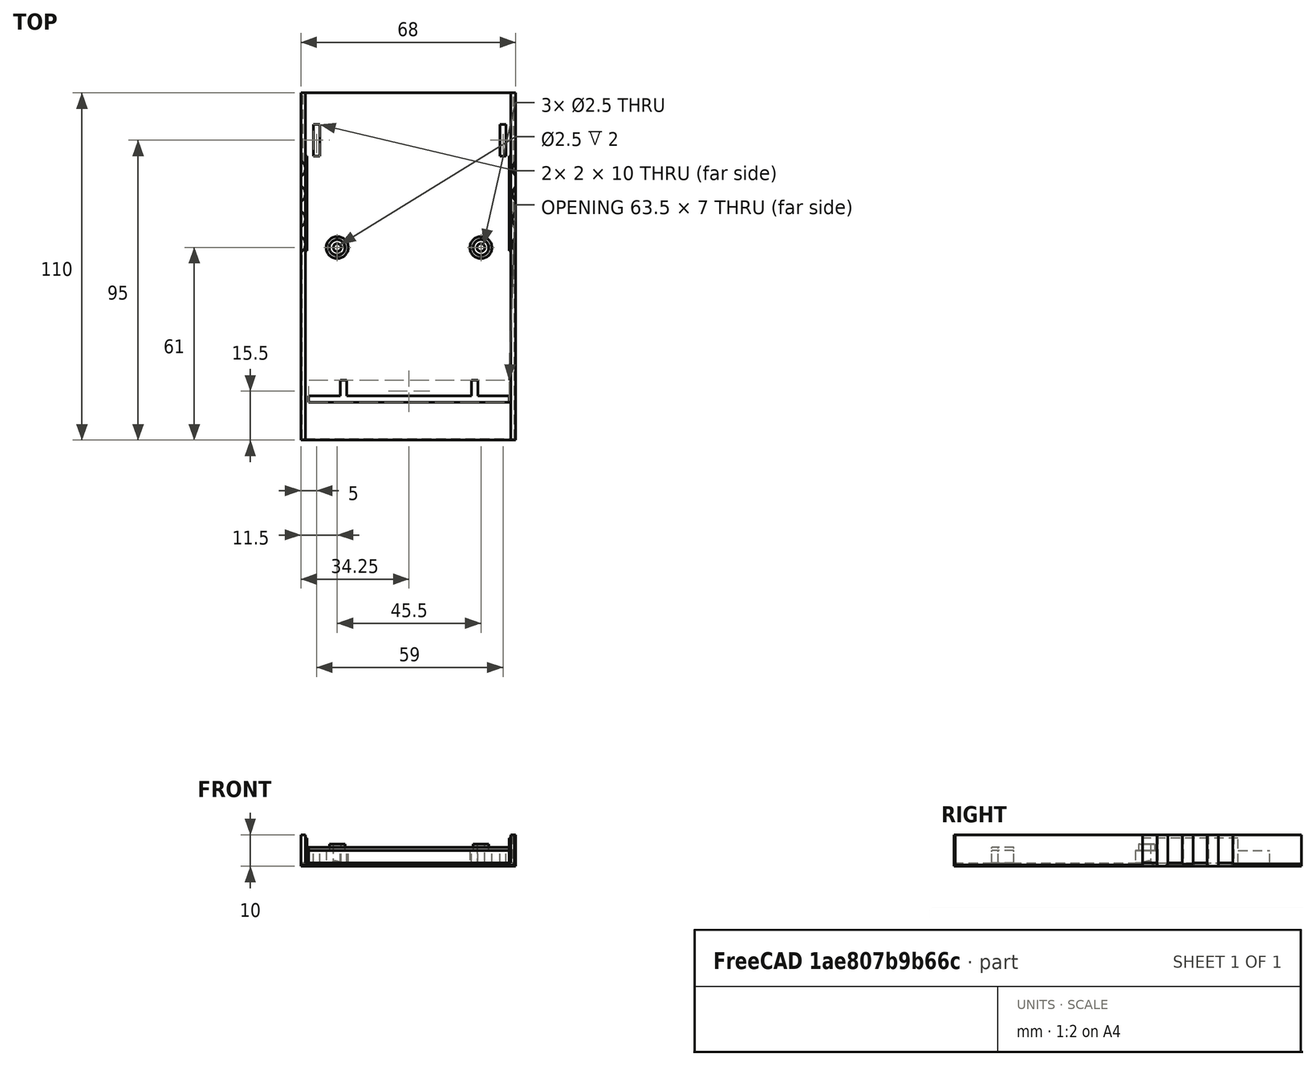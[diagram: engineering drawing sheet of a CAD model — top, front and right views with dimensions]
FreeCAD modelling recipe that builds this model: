
FCSTD DOCUMENT  (FreeCAD 0.20R29410 (Git))
Label: RTO_Cart_Bottom
License: All rights reserved
LicenseURL: http://en.wikipedia.org/wiki/All_rights_reserved
objects: Part::Cylinder×14, Part::MultiFuse×12, Part::Cut×12, Part::Box×7, Part::Chamfer×4, Part::Cone×2, Sketcher::SketchObject×1, PartDesign::Pad×1, PartDesign::Body×1, Mesh::Feature×1, Part::Feature×1
note: 56 computed .brp shape members not serialized (recipe doc carries the construction recipe); baked Part::Feature solids carry a one-line shape summary decoded from their .brp

FEATURE [Part::Cylinder] Cylinder001  label="Cilindro"
  Angle = 360
  AttacherType = Attacher::AttachEngine3D
  FirstAngle = 0
  Height = 16
  Placement = pos=(-11,61,-2) rot=(0,0,1;0rad)
  Radius = 1.25
  SecondAngle = 0
FEATURE [Part::Cylinder] Cylinder002  label="Cilindro001"
  Angle = 360
  AttacherType = Attacher::AttachEngine3D
  FirstAngle = 0
  Height = 20
  Placement = pos=(-56.5,61,-2) rot=(0,0,1;0rad)
  Radius = 1.25
  SecondAngle = 0
FEATURE [Part::Cone] Cone  label="Cono"
  Angle = 360
  AttacherType = Attacher::AttachEngine3D
  Height = 4
  Placement = pos=(-11,61,-1) rot=(0,0,1;3.14159rad)
  Radius1 = 3
  Radius2 = 0
FEATURE [Part::Cone] Cone001  label="Cono001"
  Angle = 360
  AttacherType = Attacher::AttachEngine3D
  Height = 4
  Placement = pos=(-56.7,61.2,-1) rot=(0,0,1;0.017453rad)
  Radius1 = 3
  Radius2 = 0
FEATURE [Part::Box] Box  label="Cubo"
  AttacherType = Attacher::AttachEngine3D
  Height = 4
  Length = 2
  Placement = pos=(-5,90,1) rot=(0,0,1;0rad)
  Width = 10
FEATURE [Part::Box] Box001  label="Cubo001"
  AttacherType = Attacher::AttachEngine3D
  Height = 4
  Length = 2
  Placement = pos=(-64,90,1) rot=(0,0,1;0rad)
  Width = 10
FEATURE [Part::Box] Box004  label="base"
  AttacherType = Attacher::AttachEngine3D
  Height = 1
  Length = 68
  Placement = pos=(-68,0,0) rot=(0,0,1;0rad)
  Width = 110
FEATURE [Part::Cylinder] Cylinder003  label="Cilindro002"
  Angle = 360
  AttacherType = Attacher::AttachEngine3D
  FirstAngle = 0
  Height = 4
  Placement = pos=(-11,61,1) rot=(0,0,1;0rad)
  Radius = 3.5
  SecondAngle = 0
FEATURE [Part::Cylinder] Cylinder004  label="Cilindro003"
  Angle = 360
  AttacherType = Attacher::AttachEngine3D
  FirstAngle = 0
  Height = 3
  Placement = pos=(-11,61,4) rot=(0,0,1;0rad)
  Radius = 2.5
  SecondAngle = 0
FEATURE [Part::Cylinder] Cylinder  label="Cilindro004"
  Angle = 360
  AttacherType = Attacher::AttachEngine3D
  FirstAngle = 0
  Height = 4
  Placement = pos=(-56.5,61,1) rot=(0,0,1;0rad)
  Radius = 3.5
  SecondAngle = 0
FEATURE [Part::Cylinder] Cylinder005  label="Cilindro005"
  Angle = 360
  AttacherType = Attacher::AttachEngine3D
  FirstAngle = 0
  Height = 2
  Placement = pos=(-56.5,61,5) rot=(0,0,1;0rad)
  Radius = 2.5
  SecondAngle = 0
FEATURE [Part::Box] Box005  label="Cubo002"
  AttacherType = Attacher::AttachEngine3D
  Height = 10
  Length = 1.5
  Placement = pos=(-1.5,0,0) rot=(0,0,1;0rad)
  Width = 110
FEATURE [Part::Box] Box006  label="Cubo003"
  AttacherType = Attacher::AttachEngine3D
  Height = 10
  Length = 1.5
  Placement = pos=(-68,0,0) rot=(0,0,1;0rad)
  Width = 110
FEATURE [Sketcher::SketchObject] Sketch004
  AttachmentOffset = pos=(0,0,1) rot=(0,0,1;0rad)
  FullyConstrained = true
  MapMode = 5
  Placement = pos=(0,0,1) rot=(0,0,1;0rad)
  Support = -> [XY_Plane]
  sketch-geometry (12):
    g0: LineSegment StartX=-65.5 StartY=12 StartZ=0 EndX=-2 EndY=12 EndZ=0
    g1: LineSegment StartX=-2 StartY=14 StartZ=0 EndX=-12 EndY=14 EndZ=0
    g2: LineSegment StartX=-12 StartY=19 StartZ=0 EndX=-14 EndY=19 EndZ=0
    g3: LineSegment StartX=-12 StartY=19 StartZ=0 EndX=-12 EndY=14 EndZ=0
    g4: LineSegment StartX=-14 StartY=19 StartZ=0 EndX=-14 EndY=14 EndZ=0
    g5: LineSegment StartX=-14 StartY=14 StartZ=0 EndX=-53.5 EndY=14 EndZ=0
    g6: LineSegment StartX=-53.5 StartY=14 StartZ=0 EndX=-53.5 EndY=19 EndZ=0
    g7: LineSegment StartX=-53.5 StartY=19 StartZ=0 EndX=-55.5 EndY=19 EndZ=0
    g8: LineSegment StartX=-55.5 StartY=19 StartZ=0 EndX=-55.5 EndY=14 EndZ=0
    g9: LineSegment StartX=-55.5 StartY=14 StartZ=0 EndX=-65.5 EndY=14 EndZ=0
    g10: LineSegment StartX=-65.5 StartY=14 StartZ=0 EndX=-65.5 EndY=12 EndZ=0
    g11: LineSegment StartX=-2 StartY=14 StartZ=0 EndX=-2 EndY=12 EndZ=0
  constraints (36):
    c: Horizontal(g0)
    c: Horizontal(g1)
    c: Coincident(g3,g2)
    c: Coincident(g3,g1)
    c: Coincident(g4,g2)
    c: Vertical(g4)
    c: Coincident(g5,g4)
    c: Horizontal(g5)
    c: Coincident(g6,g5)
    c: Vertical(g6)
    c: Coincident(g7,g6)
    c: Coincident(g7,g8)
    c: Vertical(g8)
    c: Coincident(g8,g9)
    c: Horizontal(g9)
    c: Coincident(g9,g10)
    c: Coincident(g10,g0)
    c: Horizontal(g7)
    c: Vertical(g10)
    c: Vertical(g3)
    c: DistanceY(g0,g9) = 2
    c: DistanceX(g7,g7) = 2
    c: DistanceX(g2,g2) = 2
    c: DistanceY(g4,g4) = 5
    c: DistanceY(g0,g1) = 2
    c: DistanceY(g8,g5) = 0
    c: Horizontal(g2)
    c: DistanceX(g0,g0) = 63.5
    c: DistanceX(g9,g9) = 10
    c: DistanceX(g1,g1) = 10
    c: DistanceY(g8,g8) = 5
    c: Coincident(g11,g1)
    c: Coincident(g11,g0)
    c: Vertical(g11)
    c: DistanceY(g-1,g0) = 12
    c: DistanceX(g0,g-1) = 2
FEATURE [PartDesign::Pad] Pad013  label="front_bar"
  Direction = (0,0,1)
  Length = 5
  Length2 = 10
  Profile = -> Sketch004
  ReferenceAxis = -> Sketch004 [N_Axis]
  Type = 0
FEATURE [Part::MultiFuse] Fusion
  Shapes = -> [Box004,Pad013]
FEATURE [Part::MultiFuse] Fusion001
  Shapes = -> [Fusion,Box]
FEATURE [Part::MultiFuse] Fusion002
  Shapes = -> [Fusion001,Box001]
FEATURE [Part::MultiFuse] Fusion003
  Shapes = -> [Fusion002,Cylinder003]
FEATURE [Part::MultiFuse] Fusion004
  Shapes = -> [Fusion003,Cylinder004]
FEATURE [Part::Cut] Cut
  Base = -> Fusion004
  Tool = -> Cylinder001
FEATURE [Part::Cut] Cut001
  Base = -> Cut
  Tool = -> Cone
FEATURE [Part::MultiFuse] Fusion005
  Shapes = -> [Cut001,Cylinder]
FEATURE [Part::MultiFuse] Fusion006
  Shapes = -> [Fusion005,Cylinder005]
FEATURE [Part::Cut] Cut002
  Base = -> Fusion006
  Tool = -> Cylinder002
FEATURE [Part::Cut] Cut003
  Base = -> Cut002
  Tool = -> Cone001
FEATURE [Part::MultiFuse] Fusion007
  Shapes = -> [Cut003,Box005]
FEATURE [Part::MultiFuse] Fusion008
  Shapes = -> [Fusion007,Box006]
FEATURE [PartDesign::Body] Body001  label="slot"
  Group = -> [Sketch004,Pad013]
  Origin = -> Origin
  Placement = pos=(0,0,-1) rot=(0,0,1;0rad)
  Tip = -> Pad013
FEATURE [Part::Cylinder] Cylinder006  label="Cilindro006"
  Angle = 360
  AttacherType = Attacher::AttachEngine3D
  FirstAngle = 0
  Height = 22
  Placement = pos=(2,62,0) rot=(0,0,1;0rad)
  Radius = 3
  SecondAngle = 0
FEATURE [Part::Cylinder] Cylinder007  label="Cilindro007"
  Angle = 360
  AttacherType = Attacher::AttachEngine3D
  FirstAngle = 0
  Height = 22
  Placement = pos=(2,70,0) rot=(0,0,1;0rad)
  Radius = 3
  SecondAngle = 0
FEATURE [Part::Cylinder] Cylinder008  label="Cilindro008"
  Angle = 360
  AttacherType = Attacher::AttachEngine3D
  FirstAngle = 0
  Height = 22
  Placement = pos=(2,78,0) rot=(0,0,1;0rad)
  Radius = 3
  SecondAngle = 0
FEATURE [Part::Cylinder] Cylinder009  label="Cilindro009"
  Angle = 360
  AttacherType = Attacher::AttachEngine3D
  FirstAngle = 0
  Height = 22
  Placement = pos=(2,86,0) rot=(0,0,1;0rad)
  Radius = 3
  SecondAngle = 0
FEATURE [Part::Cylinder] Cylinder010  label="Cilindro010"
  Angle = 360
  AttacherType = Attacher::AttachEngine3D
  FirstAngle = 0
  Height = 22
  Placement = pos=(-69.6,86,0) rot=(0,0,1;0rad)
  Radius = 3
  SecondAngle = 0
FEATURE [Part::Cylinder] Cylinder011  label="Cilindro011"
  Angle = 360
  AttacherType = Attacher::AttachEngine3D
  FirstAngle = 0
  Height = 22
  Placement = pos=(-69.6,78,0) rot=(0,0,1;0rad)
  Radius = 3
  SecondAngle = 0
FEATURE [Part::Cylinder] Cylinder012  label="Cilindro012"
  Angle = 360
  AttacherType = Attacher::AttachEngine3D
  FirstAngle = 0
  Height = 22
  Placement = pos=(-69.6,70,0) rot=(0,0,1;0rad)
  Radius = 3
  SecondAngle = 0
FEATURE [Part::Cylinder] Cylinder013  label="Cilindro013"
  Angle = 360
  AttacherType = Attacher::AttachEngine3D
  FirstAngle = 0
  Height = 22
  Placement = pos=(-69.6,62,0) rot=(0,0,1;0rad)
  Radius = 3
  SecondAngle = 0
FEATURE [Part::Box] Box007  label="Cubo004"
  AttacherType = Attacher::AttachEngine3D
  Height = 8
  Length = 1
  Placement = pos=(-67,60,1) rot=(0,0,1;0rad)
  Width = 30
FEATURE [Part::MultiFuse] Fusion009
  Shapes = -> [Fusion008,Box007]
FEATURE [Part::Box] Box008  label="Cubo005"
  AttacherType = Attacher::AttachEngine3D
  Height = 8
  Length = 1
  Placement = pos=(-2,60,1) rot=(0,0,1;0rad)
  Width = 30
FEATURE [Part::Cut] Cut004
  Base = -> Fusion009
  Tool = -> Cylinder006
FEATURE [Part::Cut] Cut006
  Base = -> Cut004
  Tool = -> Cylinder008
FEATURE [Part::Cut] Cut007
  Base = -> Cut006
  Tool = -> Cylinder009
FEATURE [Part::Cut] Cut008
  Base = -> Cut007
  Tool = -> Cylinder013
FEATURE [Part::Cut] Cut009
  Base = -> Cut008
  Tool = -> Cylinder012
FEATURE [Part::Cut] Cut010
  Base = -> Cut009
  Tool = -> Cylinder011
FEATURE [Part::Cut] Cut011
  Base = -> Cut010
  Tool = -> Cylinder010
FEATURE [Part::Cut] Cut012
  Base = -> Cut011
  Tool = -> Cylinder007
FEATURE [Part::MultiFuse] Fusion010
  Shapes = -> [Fusion005,Box008]
FEATURE [Part::MultiFuse] Fusion011
  Shapes = -> [Fusion010,Cut012]
FEATURE [Part::Chamfer] Chamfer
  Base = -> Cut012
  Edges = 4 edges r=0.7: [Edge176,Edge180,Edge181,Edge189]
FEATURE [Part::Chamfer] Chamfer001
  Base = -> Chamfer
  Edges = 2 edges r=0.4: [Edge12,Edge40]
FEATURE [Part::Chamfer] Chamfer002
  Base = -> Chamfer001
  Edges = 1 edges r=0.4: [Edge17]
FEATURE [Part::Chamfer] Chamfer003
  Base = -> Chamfer002
  Edges = 1 edges r=0.4: [Edge47]
FEATURE [Mesh::Feature] Mesh  label="Chamfer003 (Meshed)"
FEATURE [Part::Feature] Refined_Mesh_Solid_77860
  shape: bbox 68 x 110 x 10 mm, 512 faces, 0 solids (baked)
